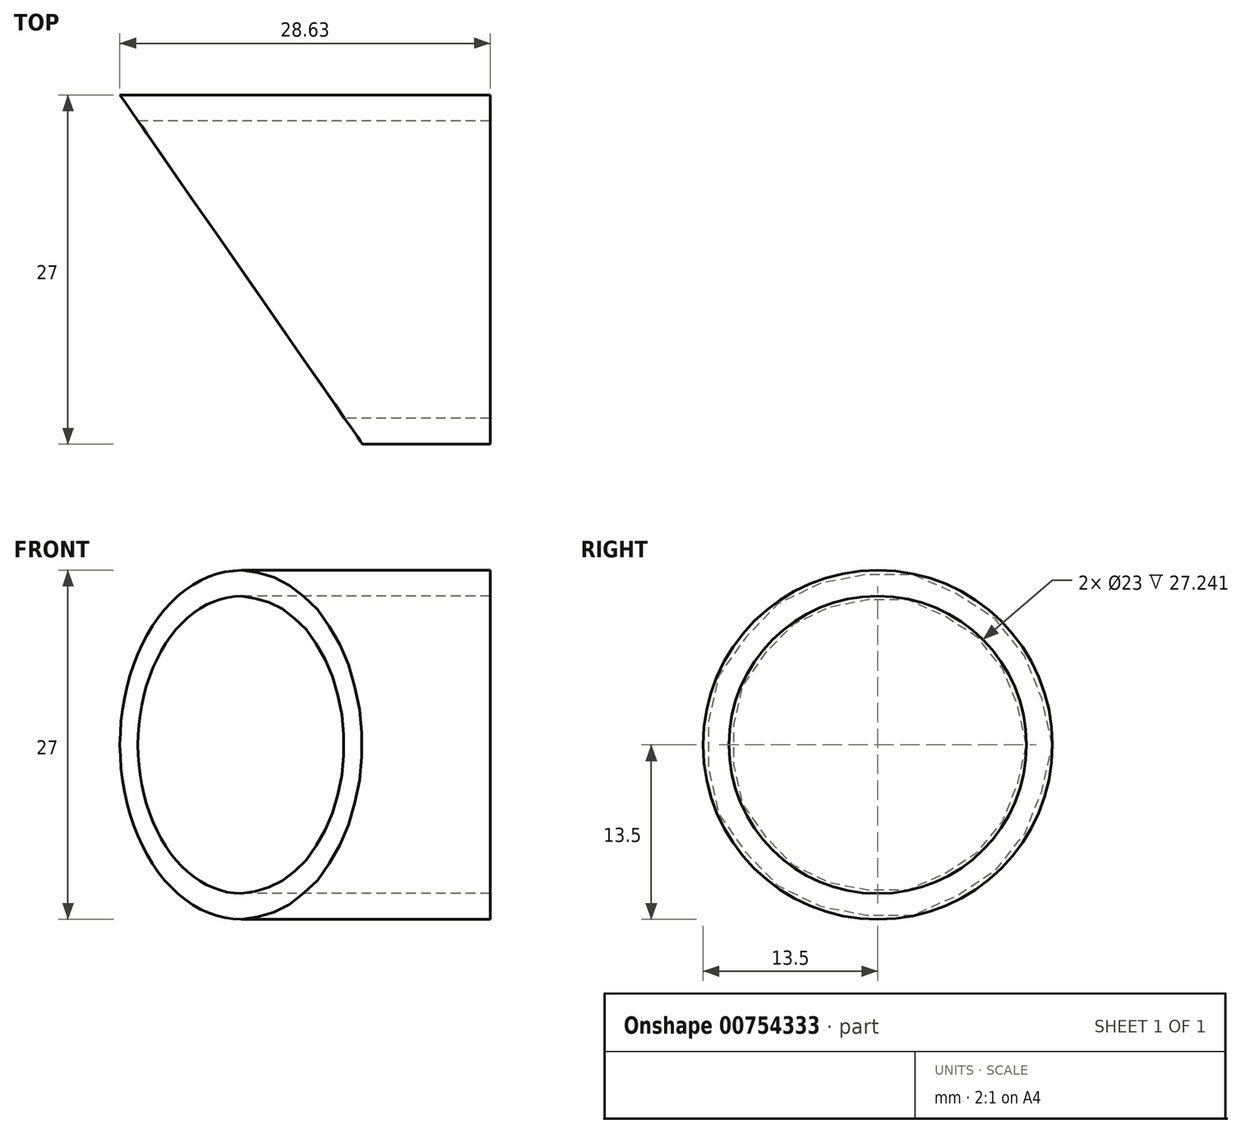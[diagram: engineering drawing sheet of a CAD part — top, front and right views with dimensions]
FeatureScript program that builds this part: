
annotation { "Feature Type Name" : "Feature", "Feature Type Description" : "" }
export const myFeature = defineFeature(function(context is Context, id is Id, definition is map)
    precondition{}
    {
        {
            var Q0;
            Q0=qCreatedBy(makeId("Right.planeOp"),FACE);
            var sketch = newSketch(context, id + "F0", { "sketchPlane" : qUnion([Q0])});
            skCircle(sketch, "E0", {"center": v(0, 0) * mm, "radius": 13.5 * mm});
            skCircle(sketch, "E1", {"center": v(0, 0) * mm, "radius": 11.5 * mm});
            skSolve(sketch);
        }
        {
            var Q0;
            Q0=qSketchRegion(id+"F0",true);
            extrude(context, id + "F1", {"entities" : qUnion([Q0]), "depth" : 28.63 * mm, "offsetDistance" : 25 * mm});
        }
        {
            var Q0;
            Q0=qCreatedBy(makeId("Top.planeOp"),FACE);
            var sketch = newSketch(context, id + "F2", { "sketchPlane" : qUnion([Q0])});
            skLineSegment(sketch, "E2", {"start": v(0, 13.5) * mm, "end": v(18.75, -13.5) * mm});
            skLineSegment(sketch, "E3", {"start": v(18.75, -13.5) * mm, "end": v(0, -13.5) * mm});
            skLineSegment(sketch, "E4", {"start": v(0, -13.5) * mm, "end": v(0, 13.5) * mm});
            skLineSegment(sketch, "E5", {"start": v(0, 0) * mm, "end": v(0, 13.5) * mm, "construction": true});
            skSolve(sketch);
        }
        {
            var Q0;
            Q0=qSketchRegion(id+"F2",true);
            extrude(context, id + "F3", {"entities" : qUnion([Q0]), "operationType" : NewBodyOperationType.REMOVE, "depth" : 25 * mm, "offsetDistance" : 25 * mm, "hasSecondDirection" : true, "secondDirectionOppositeDirection" : true, "secondDirectionDepth" : 25 * mm});
        }
    });
